# Revit family: Flushvalve-Urinal_Exposed-American_Standard-Ultima_Selectronic_6245XXX_Series
name_source: partatom
category: Plumbing Fixtures
units: mm (PartAtom-declared; Revit-internal decimal feet)

## family parameters
Always vertical = No
Cut with Voids When Loaded = No
OmniClass Number = 23.65.70.00
OmniClass Title = Terminals for Supplied Liquids and Gases
Part Type = Normal
Room Calculation Point = No
Round Connector Dimension = Use Diameter
Shared = Yes
Work Plane-Based = Yes

## types (3) — shared parameters
12-1/2" long vacuum breaker (M964446-0020A)- 4" longer than standard = No
ADA Compliant = Yes
Assembly Code = D2020300
Battery Life = 240,000 cycles (5 years @ 4,000 flushes per month)
CW Connection = Yes
CWFU = 5
Centre to Wall Distance = 2 1/4"
Connection Radius = 3/8"
Connection Size = 3/4"
Critical Line Height = 6"
Default Elevation = 0"
Description = Ultima Selectronic Exposed Urinal Flush Valve – Diaphragm-Type Battery Powered
Finish = Metal-American Standard-002-Polished Chrome
Flow Requirement = 10 gpm (37.9 L/min.)
HW Connection = No
HWFU = 5
Height = 16"
IAPMO Certification = ASSE 1037,ANSI/ASME A112.19.2
Inlet Height = 11 1/2"
Inlet Width = 4 1/4"
Inlet Width Constraint = 4 1/4"
Installation Type = Surface Mounted
Length = 2 1/4"
Manufacturer = American Standard
Material = Metal-American Standard-002-Polished Chrome
Operating Pressure = 20 psi (flowing) - 80 psi (static)
Price = Prices may vary. Please consult Sloan Rep for most up-to-date price list.
Type Comments = Inlet includes 3/4in. sweat solder kit and angle stop with back flow protection and vandal-resistant cap. Outlet includes 3/4in. high back pressure vacuum breaker with spud coupling and flange.
URL = https://www.americanstandard-us.com
Vent Connection = No
Waste Connection = No
Width = 3 3/4"
zero-valued in all types: WFU

## per-type parameters (varying)
| type | Flush Rate |
| 6245013.002 | 0.125 gpf/0.5 Lpf |
| 6245051.002 | 0.5 gpf/1.9 Lpf |
| 6245101.002 | 1.0 gpf/3.8 Lpf |

note: column(s) folded — value = type name in every type: Model

## geometry (parser evidence)
native form markers: Sweep x2
no freeform markers — native parametric forms only
